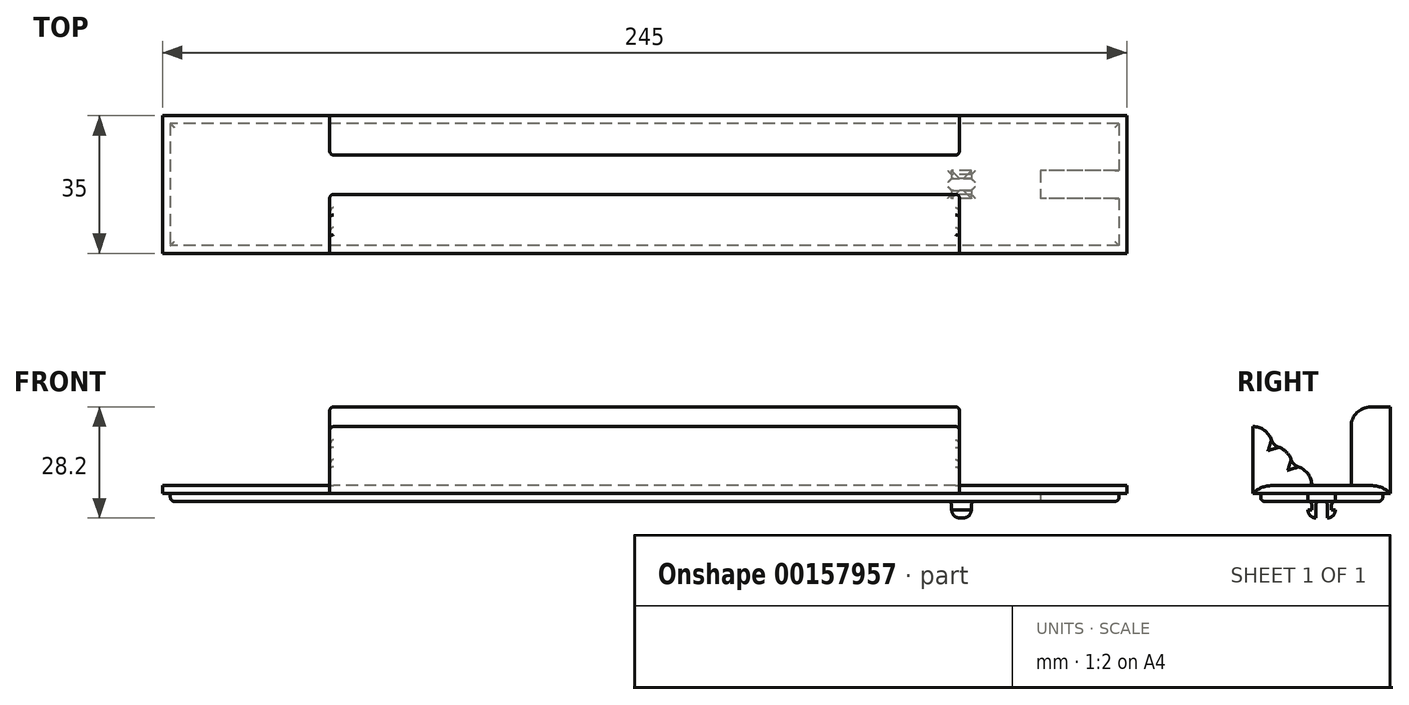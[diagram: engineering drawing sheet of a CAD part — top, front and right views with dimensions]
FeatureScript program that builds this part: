
annotation { "Feature Type Name" : "Feature", "Feature Type Description" : "" }
export const myFeature = defineFeature(function(context is Context, id is Id, definition is map)
    precondition{}
    {
        {
            var Q0;
            Q0=qCreatedBy(makeId("Right.planeOp"),FACE);
            var sketch = newSketch(context, id + "F0", { "sketchPlane" : qUnion([Q0])});
            skPoint(sketch, "E0.middle", {"position": v(0, 0) * mm});
            skLineSegment(sketch, "E1", {"start": v(18.73, 20.16) * mm, "end": v(18.73, 20.16) * mm});
            skLineSegment(sketch, "E2.bottom", {"start": v(13.13, 38.98) * mm, "end": v(22.1, 38.98) * mm});
            skPoint(sketch, "E3.visualSharp", {"position": v(11.13, 38.98) * mm});
            skArc(sketch, "E3.filletArc", {"start": v(13.13, 38.98) * mm, "mid": v(11.72, 38.4) * mm, "end": v(11.13, 36.98) * mm});
            skLineSegment(sketch, "E4.bottom", {"start": v(17.5, 1) * mm, "end": v(-17.5, 1) * mm});
            skLineSegment(sketch, "E4.top", {"start": v(17.5, -1) * mm, "end": v(-17.5, -1) * mm});
            skLineSegment(sketch, "E4.left", {"start": v(17.5, 1) * mm, "end": v(17.5, -1) * mm});
            skLineSegment(sketch, "E4.right", {"start": v(-17.5, 1) * mm, "end": v(-17.5, -1) * mm});
            skLineSegment(sketch, "E5.bottom", {"start": v(17.5, 1) * mm, "end": v(7.5, 1) * mm});
            skLineSegment(sketch, "E5.top", {"start": v(17.5, 21) * mm, "end": v(12.5, 21) * mm});
            skLineSegment(sketch, "E5.left", {"start": v(17.5, 1) * mm, "end": v(17.5, 21) * mm});
            skLineSegment(sketch, "E5.right", {"start": v(7.5, 1) * mm, "end": v(7.5, 16) * mm});
            skLineSegment(sketch, "E6.bottom", {"start": v(-17.5, 1) * mm, "end": v(-12.5, 1) * mm});
            skLineSegment(sketch, "E6.top", {"start": v(-17.5, 16) * mm, "end": v(-17.5, 16) * mm});
            skLineSegment(sketch, "E6.left", {"start": v(-17.5, 1) * mm, "end": v(-17.5, 16) * mm});
            skLineSegment(sketch, "E6.right", {"start": v(-12.5, 1) * mm, "end": v(-12.5, 11) * mm});
            skLineSegment(sketch, "E7.bottom", {"start": v(-12.5, 11) * mm, "end": v(-12.5, 11) * mm});
            skLineSegment(sketch, "E7.top", {"start": v(-12.5, 1) * mm, "end": v(-7.5, 1) * mm});
            skLineSegment(sketch, "E7.left", {"start": v(-12.5, 11) * mm, "end": v(-12.5, 1) * mm});
            skLineSegment(sketch, "E7.right", {"start": v(-7.5, 6) * mm, "end": v(-7.5, 1) * mm});
            skLineSegment(sketch, "E8.bottom", {"start": v(-7.5, 6) * mm, "end": v(-7.5, 6) * mm});
            skLineSegment(sketch, "E8.top", {"start": v(-7.5, 1) * mm, "end": v(-2.5, 1) * mm});
            skLineSegment(sketch, "E8.right", {"start": v(-2.5, 1) * mm, "end": v(-2.5, 1) * mm});
            skPoint(sketch, "E9.visualSharp", {"position": v(7.5, 21) * mm});
            skArc(sketch, "E9.filletArc", {"start": v(12.5, 21) * mm, "mid": v(8.96, 19.54) * mm, "end": v(7.5, 16) * mm});
            skPoint(sketch, "E10.visualSharp", {"position": v(-2.5, 6) * mm});
            skArc(sketch, "E10.filletArc", {"start": v(-2.5, 1) * mm, "mid": v(-3.96, 4.54) * mm, "end": v(-7.5, 6) * mm});
            skPoint(sketch, "E11.visualSharp", {"position": v(-7.5, 11) * mm});
            skArc(sketch, "E11.filletArc", {"start": v(-7.5, 6) * mm, "mid": v(-8.96, 9.54) * mm, "end": v(-12.5, 11) * mm});
            skPoint(sketch, "E12.visualSharp", {"position": v(-12.5, 16) * mm});
            skArc(sketch, "E12.filletArc", {"start": v(-12.5, 11) * mm, "mid": v(-13.96, 14.54) * mm, "end": v(-17.5, 16) * mm});
            skSolve(sketch);
        }
        {
            var Q0;
            Q0=makeQuery(id+"F0.imprint","IMPRINT",FACE,{"disambiguationData":[TD([[makeQuery(id+"F0.imprint","IMPRINT",EDGE,{"derivedFrom":sQuery(id+"F0.wireOp",EDGE,"E5.top")}),1.0]])]});
            var Q1;
            Q1=makeQuery(id+"F0.imprint","IMPRINT",FACE,{"disambiguationData":[TD([[makeQuery(id+"F0.imprint","IMPRINT",EDGE,{"derivedFrom":sQuery(id+"F0.wireOp",EDGE,"E4.top")}),-1.0]])]});
            var Q2;
            {var subQ0=sQuery(id+"F0.wireOp",EDGE,"E6.left");Q2=makeQuery(id+"F0.imprint","IMPRINT",FACE,{"disambiguationData":[TD([[makeQuery(id+"F0.imprint","IMPRINT",EDGE,{"derivedFrom":subQ0}),-1.0]])]});}
            var Q3;
            {var subQ2=sQuery(id+"F0.wireOp",EDGE,"E6.right");Q3=makeQuery(id+"F0.imprint","IMPRINT",FACE,{"disambiguationData":[TD([[makeQuery(id+"F0.imprint","IMPRINT",EDGE,{"derivedFrom":subQ2}),-1.0]])]});}
            var Q4;
            {var subQ0=sQuery(id+"F0.wireOp",EDGE,"E7.right");Q4=makeQuery(id+"F0.imprint","IMPRINT",FACE,{"disambiguationData":[TD([[makeQuery(id+"F0.imprint","IMPRINT",EDGE,{"derivedFrom":subQ0}),1.0]])]});}
            extrude(context, id + "F1", {"entities" : qUnion([Q0, Q1, Q2, Q3, Q4]), "endBound" : BoundingType.SYMMETRIC, "depth" : 245 * mm});
        }
        {
            var Q0;
            Q0=makeQuery(id+"F1.opExtrude","SWEPT_FACE",FACE,{"disambiguationData":[OSD([sQuery(id+"F0.wireOp",EDGE,"E4.top")])]});
            var sketch = newSketch(context, id + "F2", { "sketchPlane" : qUnion([Q0])});
            skLineSegment(sketch, "E13.bottom", {"start": v(120.5, -15.5) * mm, "end": v(-120.5, -15.5) * mm});
            skLineSegment(sketch, "E13.top", {"start": v(120.5, 15.5) * mm, "end": v(-120.5, 15.5) * mm});
            skLineSegment(sketch, "E13.left", {"start": v(120.5, -15.5) * mm, "end": v(120.5, 15.5) * mm});
            skLineSegment(sketch, "E13.right", {"start": v(-120.5, -15.5) * mm, "end": v(-120.5, 15.5) * mm});
            skPoint(sketch, "E13.middle", {"position": v(0, 0) * mm});
            skSolve(sketch);
        }
        {
            var Q0;
            Q0=qSketchRegion(id+"F2",true);
            extrude(context, id + "F3", {"entities" : qUnion([Q0]), "operationType" : NewBodyOperationType.ADD, "depth" : 2 * mm});
        }
        {
            var Q0;
            Q0=makeQuery(id+"F3.opExtrude","CAP_FACE",FACE,{"disambiguationData":[OSD([sQuery(id+"F2.wireOp",EDGE,"E13.bottom"),sQuery(id+"F2.wireOp",EDGE,"E13.top"),sQuery(id+"F2.wireOp",EDGE,"E13.left"),sQuery(id+"F2.wireOp",EDGE,"E13.right")])],"isStart":false});
            var sketch = newSketch(context, id + "F4", { "sketchPlane" : qUnion([Q0])});
            skLineSegment(sketch, "E14.bottom", {"start": v(83, -2.5) * mm, "end": v(78, -2.5) * mm});
            skLineSegment(sketch, "E14.top", {"start": v(83, 2.5) * mm, "end": v(78, 2.5) * mm});
            skLineSegment(sketch, "E14.left", {"start": v(83, -2.5) * mm, "end": v(83, 2.5) * mm});
            skLineSegment(sketch, "E14.right", {"start": v(78, -2.5) * mm, "end": v(78, 2.5) * mm});
            skPoint(sketch, "E14.middle", {"position": v(80.5, 0) * mm});
            skPoint(sketch, "E15", {"position": v(120.5, -0.48) * mm});
            skSolve(sketch);
        }
        {
            var Q0;
            Q0=qSketchRegion(id+"F4",true);
            extrude(context, id + "F5", {"entities" : qUnion([Q0]), "operationType" : NewBodyOperationType.ADD, "depth" : 2.2 * mm});
        }
        {
            var Q0;
            Q0=makeQuery(id+"F5.opExtrude","CAP_FACE",FACE,{"disambiguationData":[OSD([sQuery(id+"F4.wireOp",EDGE,"E14.bottom"),sQuery(id+"F4.wireOp",EDGE,"E14.top"),sQuery(id+"F4.wireOp",EDGE,"E14.left"),sQuery(id+"F4.wireOp",EDGE,"E14.right")])],"isStart":false});
            var sketch = newSketch(context, id + "F6", { "sketchPlane" : qUnion([Q0])});
            skLineSegment(sketch, "E16.bottom", {"start": v(83, 3.5) * mm, "end": v(78, 3.5) * mm});
            skLineSegment(sketch, "E16.top", {"start": v(83, -3.5) * mm, "end": v(78, -3.5) * mm});
            skLineSegment(sketch, "E16.left", {"start": v(78, 3.5) * mm, "end": v(78, -3.5) * mm});
            skLineSegment(sketch, "E16.right", {"start": v(83, 3.5) * mm, "end": v(83, -3.5) * mm});
            skPoint(sketch, "E16.middle.positionSnap0", {"position": v(83, 0) * mm});
            skPoint(sketch, "E16.centerSnap0", {"position": v(83, 0) * mm});
            skPoint(sketch, "E17", {"position": v(78, 0) * mm});
            skSolve(sketch);
        }
        {
            var Q0;
            Q0=qSketchRegion(id+"F6",true);
            extrude(context, id + "F7", {"entities" : qUnion([Q0]), "operationType" : NewBodyOperationType.ADD, "depth" : 2 * mm});
        }
        {
            var Q0;
            Q0=makeQuery(id+"F7.opExtrude","CAP_FACE",FACE,{"disambiguationData":[OSD([sQuery(id+"F6.wireOp",EDGE,"E16.bottom"),sQuery(id+"F6.wireOp",EDGE,"E16.top"),sQuery(id+"F6.wireOp",EDGE,"E16.left"),sQuery(id+"F6.wireOp",EDGE,"E16.right")])],"isStart":false});
            var sketch = newSketch(context, id + "F8", { "sketchPlane" : qUnion([Q0])});
            skLineSegment(sketch, "E18.bottom", {"start": v(83, 1.5) * mm, "end": v(78, 1.5) * mm});
            skLineSegment(sketch, "E18.top", {"start": v(83, -1.5) * mm, "end": v(78, -1.5) * mm});
            skLineSegment(sketch, "E18.left", {"start": v(78, 1.5) * mm, "end": v(78, -1.5) * mm});
            skLineSegment(sketch, "E18.right", {"start": v(83, 1.5) * mm, "end": v(83, -1.5) * mm});
            skLineSegment(sketch, "E19.bottom", {"start": v(39.5, -3.5) * mm, "end": v(36.5, -3.5) * mm});
            skSolve(sketch);
        }
        {
            var Q0;
            Q0=makeQuery(id+"F8.imprint","IMPRINT",FACE,{"disambiguationData":[TD([[makeQuery(id+"F8.imprint","IMPRINT",EDGE,{"derivedFrom":sQuery(id+"F8.wireOp",EDGE,"E18.bottom")}),1.0]])]});
            extrude(context, id + "F9", {"entities" : qUnion([Q0]), "operationType" : NewBodyOperationType.REMOVE, "oppositeDirection" : true, "depth" : 4.2 * mm});
        }
        {
            var Q0;
            {var subQ0=sQuery(id+"F6.wireOp",EDGE,"E16.right");var subQ1=sQuery(id+"F6.wireOp",EDGE,"E16.top");var subQ3=makeQuery(id+"F7.opExtrude","CAP_EDGE",EDGE,{"disambiguationData":[OSD([subQ0])],"isStart":false});Q0=makeQuery(id+"F9.boolean.opBoolean","SPLIT",EDGE,{"disambiguationData":[TD([makeQuery(id+"F7.opExtrude","SWEPT_FACE",FACE,{"disambiguationData":[OSD([subQ1])]})])],"derivedFrom":subQ3});}
            var Q1;
            {var subQ0=sQuery(id+"F6.wireOp",EDGE,"E16.right");var subQ1=sQuery(id+"F6.wireOp",EDGE,"E16.top");var subQ3=makeQuery(id+"F7.opExtrude","CAP_EDGE",EDGE,{"disambiguationData":[OSD([subQ1])],"isStart":false});Q1=makeQuery(id+"F9.boolean.opBoolean","SPLIT",EDGE,{"disambiguationData":[TD([makeQuery(id+"F7.opExtrude","SWEPT_FACE",FACE,{"disambiguationData":[OSD([subQ0])]})])],"derivedFrom":subQ3});}
            var Q2;
            {var subQ0=sQuery(id+"F6.wireOp",EDGE,"E16.bottom");var subQ1=sQuery(id+"F6.wireOp",EDGE,"E16.right");var subQ3=makeQuery(id+"F7.opExtrude","CAP_EDGE",EDGE,{"disambiguationData":[OSD([subQ1])],"isStart":false});Q2=makeQuery(id+"F9.boolean.opBoolean","SPLIT",EDGE,{"disambiguationData":[TD([makeQuery(id+"F7.opExtrude","SWEPT_FACE",FACE,{"disambiguationData":[OSD([subQ0])]})])],"derivedFrom":subQ3});}
            var Q3;
            {var subQ0=sQuery(id+"F6.wireOp",EDGE,"E16.bottom");var subQ1=sQuery(id+"F6.wireOp",EDGE,"E16.right");var subQ3=makeQuery(id+"F7.opExtrude","CAP_EDGE",EDGE,{"disambiguationData":[OSD([subQ0])],"isStart":false});Q3=makeQuery(id+"F9.boolean.opBoolean","SPLIT",EDGE,{"disambiguationData":[TD([makeQuery(id+"F7.opExtrude","SWEPT_FACE",FACE,{"disambiguationData":[OSD([subQ1])]})])],"derivedFrom":subQ3});}
            var Q4;
            {var subQ0=sQuery(id+"F6.wireOp",EDGE,"E16.bottom");var subQ1=sQuery(id+"F6.wireOp",EDGE,"E16.left");var subQ3=makeQuery(id+"F7.opExtrude","CAP_EDGE",EDGE,{"disambiguationData":[OSD([subQ0])],"isStart":false});Q4=makeQuery(id+"F9.boolean.opBoolean","SPLIT",EDGE,{"disambiguationData":[TD([makeQuery(id+"F7.opExtrude","SWEPT_FACE",FACE,{"disambiguationData":[OSD([subQ1])]})])],"derivedFrom":subQ3});}
            var Q5;
            {var subQ0=sQuery(id+"F6.wireOp",EDGE,"E16.bottom");var subQ1=sQuery(id+"F6.wireOp",EDGE,"E16.left");var subQ3=makeQuery(id+"F7.opExtrude","CAP_EDGE",EDGE,{"disambiguationData":[OSD([subQ1])],"isStart":false});Q5=makeQuery(id+"F9.boolean.opBoolean","SPLIT",EDGE,{"disambiguationData":[TD([makeQuery(id+"F7.opExtrude","SWEPT_FACE",FACE,{"disambiguationData":[OSD([subQ0])]})])],"derivedFrom":subQ3});}
            var Q6;
            {var subQ0=sQuery(id+"F6.wireOp",EDGE,"E16.left");var subQ1=sQuery(id+"F6.wireOp",EDGE,"E16.top");var subQ3=makeQuery(id+"F7.opExtrude","CAP_EDGE",EDGE,{"disambiguationData":[OSD([subQ0])],"isStart":false});Q6=makeQuery(id+"F9.boolean.opBoolean","SPLIT",EDGE,{"disambiguationData":[TD([makeQuery(id+"F7.opExtrude","SWEPT_FACE",FACE,{"disambiguationData":[OSD([subQ1])]})])],"derivedFrom":subQ3});}
            var Q7;
            {var subQ0=sQuery(id+"F6.wireOp",EDGE,"E16.left");var subQ1=sQuery(id+"F6.wireOp",EDGE,"E16.top");var subQ3=makeQuery(id+"F7.opExtrude","CAP_EDGE",EDGE,{"disambiguationData":[OSD([subQ1])],"isStart":false});Q7=makeQuery(id+"F9.boolean.opBoolean","SPLIT",EDGE,{"disambiguationData":[TD([makeQuery(id+"F7.opExtrude","SWEPT_FACE",FACE,{"disambiguationData":[OSD([subQ0])]})])],"derivedFrom":subQ3});}
            fillet(context, id + "F10", {"entities" : qUnion([Q0, Q1, Q2, Q3, Q4, Q5, Q6, Q7]), "radius" : 2 * mm, "tangentPropagation" : true, "allowEdgeOverflow" : false});
        }
        {
            var Q0;
            Q0=makeQuery(id+"F9.boolean.opBoolean","MERGE",FACE,{"derivedFrom":[makeQuery(id+"F3.opExtrude","CAP_FACE",FACE,{"disambiguationData":[OSD([sQuery(id+"F2.wireOp",EDGE,"E13.bottom"),sQuery(id+"F2.wireOp",EDGE,"E13.top"),sQuery(id+"F2.wireOp",EDGE,"E13.left"),sQuery(id+"F2.wireOp",EDGE,"E13.right")])],"isStart":false}),makeQuery(id+"F9.opExtrude","CAP_FACE",FACE,{"disambiguationData":[OSD([sQuery(id+"F8.wireOp",EDGE,"E18.bottom"),sQuery(id+"F8.wireOp",EDGE,"E18.top"),sQuery(id+"F8.wireOp",EDGE,"E18.left"),sQuery(id+"F8.wireOp",EDGE,"E18.right")])],"isStart":false})]});
            fillet(context, id + "F11", {"entities" : qUnion([Q0]), "radius" : 1 * mm, "tangentPropagation" : true, "allowEdgeOverflow" : false});
        }
        {
            var Q0;
            Q0=makeQuery(id+"F1.opExtrude","CAP_FACE",FACE,{"disambiguationData":[OSD([sQuery(id+"F0.wireOp",EDGE,"E4.bottom"),sQuery(id+"F0.wireOp",EDGE,"E4.top"),sQuery(id+"F0.wireOp",EDGE,"E4.left"),sQuery(id+"F0.wireOp",EDGE,"E4.right"),sQuery(id+"F0.wireOp",EDGE,"E5.top"),sQuery(id+"F0.wireOp",EDGE,"E5.left"),sQuery(id+"F0.wireOp",EDGE,"E5.right"),sQuery(id+"F0.wireOp",EDGE,"E6.left"),sQuery(id+"F0.wireOp",EDGE,"E9.filletArc"),sQuery(id+"F0.wireOp",EDGE,"E10.filletArc"),sQuery(id+"F0.wireOp",EDGE,"E11.filletArc"),sQuery(id+"F0.wireOp",EDGE,"E12.filletArc")])],"isStart":false});
            var sketch = newSketch(context, id + "F12", { "sketchPlane" : qUnion([Q0])});
            skLineSegment(sketch, "E20.bottom", {"start": v(18.32, 21.85) * mm, "end": v(-19.38, 21.85) * mm});
            skLineSegment(sketch, "E20.top", {"start": v(18.32, 1) * mm, "end": v(-19.38, 1) * mm});
            skLineSegment(sketch, "E20.left", {"start": v(18.32, 21.85) * mm, "end": v(18.32, 1) * mm});
            skLineSegment(sketch, "E20.right", {"start": v(-19.38, 21.85) * mm, "end": v(-19.38, 1) * mm});
            skSolve(sketch);
        }
        {
            var Q0;
            Q0=qSketchRegion(id+"F12",true);
            extrude(context, id + "F13", {"entities" : qUnion([Q0]), "operationType" : NewBodyOperationType.REMOVE, "oppositeDirection" : true, "depth" : 42.5 * mm});
        }
        {
            var Q0;
            Q0=makeQuery(id+"F1.opExtrude","CAP_FACE",FACE,{"disambiguationData":[OSD([sQuery(id+"F0.wireOp",EDGE,"E4.bottom"),sQuery(id+"F0.wireOp",EDGE,"E4.top"),sQuery(id+"F0.wireOp",EDGE,"E4.left"),sQuery(id+"F0.wireOp",EDGE,"E4.right"),sQuery(id+"F0.wireOp",EDGE,"E5.top"),sQuery(id+"F0.wireOp",EDGE,"E5.left"),sQuery(id+"F0.wireOp",EDGE,"E5.right"),sQuery(id+"F0.wireOp",EDGE,"E6.left"),sQuery(id+"F0.wireOp",EDGE,"E9.filletArc"),sQuery(id+"F0.wireOp",EDGE,"E10.filletArc"),sQuery(id+"F0.wireOp",EDGE,"E11.filletArc"),sQuery(id+"F0.wireOp",EDGE,"E12.filletArc")])],"isStart":true});
            var sketch = newSketch(context, id + "F14", { "sketchPlane" : qUnion([Q0])});
            skLineSegment(sketch, "E21.bottom", {"start": v(-18.97, 22.74) * mm, "end": v(19.2, 22.74) * mm});
            skLineSegment(sketch, "E21.top", {"start": v(-18.97, 1) * mm, "end": v(19.2, 1) * mm});
            skLineSegment(sketch, "E21.left", {"start": v(-18.97, 22.74) * mm, "end": v(-18.97, 1) * mm});
            skLineSegment(sketch, "E21.right", {"start": v(19.2, 22.74) * mm, "end": v(19.2, 1) * mm});
            skSolve(sketch);
        }
        {
            var Q0;
            Q0=qSketchRegion(id+"F14",true);
            extrude(context, id + "F15", {"entities" : qUnion([Q0]), "operationType" : NewBodyOperationType.REMOVE, "oppositeDirection" : true, "depth" : 42.5 * mm});
        }
        {
            var Q0;
            Q0=makeQuery(id+"F13.boolean.opBoolean","INTERSECT",EDGE,{"derivedFrom":[makeQuery(id+"F1.opExtrude","SWEPT_FACE",FACE,{"disambiguationData":[OSD([sQuery(id+"F0.wireOp",EDGE,"E4.left"),sQuery(id+"F0.wireOp",EDGE,"E5.left")])]}),makeQuery(id+"F13.opExtrude","SWEPT_FACE",FACE,{"disambiguationData":[OSD([sQuery(id+"F12.wireOp",EDGE,"E20.top")])]})]});
            var Q1;
            Q1=makeQuery(id+"F13.boolean.opBoolean","MERGE",EDGE,{"derivedFrom":[makeQuery(id+"F1.opExtrude","CAP_EDGE",EDGE,{"disambiguationData":[OSD([sQuery(id+"F0.wireOp",EDGE,"E4.bottom")])],"isStart":false})],"fromTools":[makeQuery(id+"F13.opExtrude","CAP_EDGE",EDGE,{"disambiguationData":[OSD([sQuery(id+"F12.wireOp",EDGE,"E20.top")])],"isStart":true})]});
            var Q2;
            Q2=makeQuery(id+"F13.boolean.opBoolean","INTERSECT",EDGE,{"derivedFrom":[makeQuery(id+"F1.opExtrude","SWEPT_FACE",FACE,{"disambiguationData":[OSD([sQuery(id+"F0.wireOp",EDGE,"E4.right"),sQuery(id+"F0.wireOp",EDGE,"E6.left")])]}),makeQuery(id+"F13.opExtrude","SWEPT_FACE",FACE,{"disambiguationData":[OSD([sQuery(id+"F12.wireOp",EDGE,"E20.top")])]})]});
            var Q3;
            Q3=makeQuery(id+"F15.boolean.opBoolean","INTERSECT",EDGE,{"derivedFrom":[makeQuery(id+"F1.opExtrude","SWEPT_FACE",FACE,{"disambiguationData":[OSD([sQuery(id+"F0.wireOp",EDGE,"E4.left"),sQuery(id+"F0.wireOp",EDGE,"E5.left")])]}),makeQuery(id+"F15.opExtrude","SWEPT_FACE",FACE,{"disambiguationData":[OSD([sQuery(id+"F14.wireOp",EDGE,"E21.top")])]})]});
            var Q4;
            Q4=makeQuery(id+"F15.boolean.opBoolean","MERGE",EDGE,{"derivedFrom":[makeQuery(id+"F1.opExtrude","CAP_EDGE",EDGE,{"disambiguationData":[OSD([sQuery(id+"F0.wireOp",EDGE,"E4.bottom")])],"isStart":true})],"fromTools":[makeQuery(id+"F15.opExtrude","CAP_EDGE",EDGE,{"disambiguationData":[OSD([sQuery(id+"F14.wireOp",EDGE,"E21.top")])],"isStart":true})]});
            var Q5;
            Q5=makeQuery(id+"F15.boolean.opBoolean","INTERSECT",EDGE,{"derivedFrom":[makeQuery(id+"F1.opExtrude","SWEPT_FACE",FACE,{"disambiguationData":[OSD([sQuery(id+"F0.wireOp",EDGE,"E4.right"),sQuery(id+"F0.wireOp",EDGE,"E6.left")])]}),makeQuery(id+"F15.opExtrude","SWEPT_FACE",FACE,{"disambiguationData":[OSD([sQuery(id+"F14.wireOp",EDGE,"E21.top")])]})]});
            fillet(context, id + "F16", {"entities" : qUnion([Q0, Q1, Q2, Q3, Q4, Q5]), "radius" : 7 * mm, "tangentPropagation" : true, "allowEdgeOverflow" : false});
        }
        {
            var Q0;
            Q0=makeQuery(id+"F15.boolean.opBoolean","INTERSECT",EDGE,{"derivedFrom":[makeQuery(id+"F1.opExtrude","SWEPT_FACE",FACE,{"disambiguationData":[OSD([sQuery(id+"F0.wireOp",EDGE,"E9.filletArc")])]}),makeQuery(id+"F15.opExtrude","CAP_FACE",FACE,{"disambiguationData":[OSD([sQuery(id+"F14.wireOp",EDGE,"E21.bottom"),sQuery(id+"F14.wireOp",EDGE,"E21.top"),sQuery(id+"F14.wireOp",EDGE,"E21.left"),sQuery(id+"F14.wireOp",EDGE,"E21.right")])],"isStart":false})]});
            var Q1;
            Q1=makeQuery(id+"F15.boolean.opBoolean","INTERSECT",EDGE,{"derivedFrom":[makeQuery(id+"F1.opExtrude","SWEPT_FACE",FACE,{"disambiguationData":[OSD([sQuery(id+"F0.wireOp",EDGE,"E5.right")])]}),makeQuery(id+"F15.opExtrude","CAP_FACE",FACE,{"disambiguationData":[OSD([sQuery(id+"F14.wireOp",EDGE,"E21.bottom"),sQuery(id+"F14.wireOp",EDGE,"E21.top"),sQuery(id+"F14.wireOp",EDGE,"E21.left"),sQuery(id+"F14.wireOp",EDGE,"E21.right")])],"isStart":false})]});
            var Q2;
            Q2=makeQuery(id+"F15.boolean.opBoolean","INTERSECT",EDGE,{"derivedFrom":[makeQuery(id+"F1.opExtrude","SWEPT_FACE",FACE,{"disambiguationData":[OSD([sQuery(id+"F0.wireOp",EDGE,"E10.filletArc")])]}),makeQuery(id+"F15.opExtrude","CAP_FACE",FACE,{"disambiguationData":[OSD([sQuery(id+"F14.wireOp",EDGE,"E21.bottom"),sQuery(id+"F14.wireOp",EDGE,"E21.top"),sQuery(id+"F14.wireOp",EDGE,"E21.left"),sQuery(id+"F14.wireOp",EDGE,"E21.right")])],"isStart":false})]});
            var Q3;
            Q3=makeQuery(id+"F15.boolean.opBoolean","INTERSECT",EDGE,{"derivedFrom":[makeQuery(id+"F1.opExtrude","SWEPT_FACE",FACE,{"disambiguationData":[OSD([sQuery(id+"F0.wireOp",EDGE,"E11.filletArc")])]}),makeQuery(id+"F15.opExtrude","CAP_FACE",FACE,{"disambiguationData":[OSD([sQuery(id+"F14.wireOp",EDGE,"E21.bottom"),sQuery(id+"F14.wireOp",EDGE,"E21.top"),sQuery(id+"F14.wireOp",EDGE,"E21.left"),sQuery(id+"F14.wireOp",EDGE,"E21.right")])],"isStart":false})]});
            var Q4;
            Q4=makeQuery(id+"F15.boolean.opBoolean","INTERSECT",EDGE,{"derivedFrom":[makeQuery(id+"F1.opExtrude","SWEPT_FACE",FACE,{"disambiguationData":[OSD([sQuery(id+"F0.wireOp",EDGE,"E12.filletArc")])]}),makeQuery(id+"F15.opExtrude","CAP_FACE",FACE,{"disambiguationData":[OSD([sQuery(id+"F14.wireOp",EDGE,"E21.bottom"),sQuery(id+"F14.wireOp",EDGE,"E21.top"),sQuery(id+"F14.wireOp",EDGE,"E21.left"),sQuery(id+"F14.wireOp",EDGE,"E21.right")])],"isStart":false})]});
            var Q5;
            Q5=makeQuery(id+"F13.boolean.opBoolean","INTERSECT",EDGE,{"derivedFrom":[makeQuery(id+"F1.opExtrude","SWEPT_FACE",FACE,{"disambiguationData":[OSD([sQuery(id+"F0.wireOp",EDGE,"E12.filletArc")])]}),makeQuery(id+"F13.opExtrude","CAP_FACE",FACE,{"disambiguationData":[OSD([sQuery(id+"F12.wireOp",EDGE,"E20.bottom"),sQuery(id+"F12.wireOp",EDGE,"E20.top"),sQuery(id+"F12.wireOp",EDGE,"E20.left"),sQuery(id+"F12.wireOp",EDGE,"E20.right")])],"isStart":false})]});
            var Q6;
            Q6=makeQuery(id+"F13.boolean.opBoolean","INTERSECT",EDGE,{"derivedFrom":[makeQuery(id+"F1.opExtrude","SWEPT_FACE",FACE,{"disambiguationData":[OSD([sQuery(id+"F0.wireOp",EDGE,"E11.filletArc")])]}),makeQuery(id+"F13.opExtrude","CAP_FACE",FACE,{"disambiguationData":[OSD([sQuery(id+"F12.wireOp",EDGE,"E20.bottom"),sQuery(id+"F12.wireOp",EDGE,"E20.top"),sQuery(id+"F12.wireOp",EDGE,"E20.left"),sQuery(id+"F12.wireOp",EDGE,"E20.right")])],"isStart":false})]});
            var Q7;
            Q7=makeQuery(id+"F13.boolean.opBoolean","INTERSECT",EDGE,{"derivedFrom":[makeQuery(id+"F1.opExtrude","SWEPT_FACE",FACE,{"disambiguationData":[OSD([sQuery(id+"F0.wireOp",EDGE,"E10.filletArc")])]}),makeQuery(id+"F13.opExtrude","CAP_FACE",FACE,{"disambiguationData":[OSD([sQuery(id+"F12.wireOp",EDGE,"E20.bottom"),sQuery(id+"F12.wireOp",EDGE,"E20.top"),sQuery(id+"F12.wireOp",EDGE,"E20.left"),sQuery(id+"F12.wireOp",EDGE,"E20.right")])],"isStart":false})]});
            var Q8;
            Q8=makeQuery(id+"F13.boolean.opBoolean","INTERSECT",EDGE,{"derivedFrom":[makeQuery(id+"F1.opExtrude","SWEPT_FACE",FACE,{"disambiguationData":[OSD([sQuery(id+"F0.wireOp",EDGE,"E5.right")])]}),makeQuery(id+"F13.opExtrude","CAP_FACE",FACE,{"disambiguationData":[OSD([sQuery(id+"F12.wireOp",EDGE,"E20.bottom"),sQuery(id+"F12.wireOp",EDGE,"E20.top"),sQuery(id+"F12.wireOp",EDGE,"E20.left"),sQuery(id+"F12.wireOp",EDGE,"E20.right")])],"isStart":false})]});
            var Q9;
            Q9=makeQuery(id+"F13.boolean.opBoolean","INTERSECT",EDGE,{"derivedFrom":[makeQuery(id+"F1.opExtrude","SWEPT_FACE",FACE,{"disambiguationData":[OSD([sQuery(id+"F0.wireOp",EDGE,"E9.filletArc")])]}),makeQuery(id+"F13.opExtrude","CAP_FACE",FACE,{"disambiguationData":[OSD([sQuery(id+"F12.wireOp",EDGE,"E20.bottom"),sQuery(id+"F12.wireOp",EDGE,"E20.top"),sQuery(id+"F12.wireOp",EDGE,"E20.left"),sQuery(id+"F12.wireOp",EDGE,"E20.right")])],"isStart":false})]});
            fillet(context, id + "F17", {"entities" : qUnion([Q0, Q1, Q2, Q3, Q4, Q5, Q6, Q7, Q8, Q9]), "radius" : 1 * mm, "tangentPropagation" : true, "allowEdgeOverflow" : false});
        }
        {
            var Q0;
            Q0=makeQuery(id+"F9.boolean.opBoolean","MERGE",FACE,{"derivedFrom":[makeQuery(id+"F3.opExtrude","CAP_FACE",FACE,{"disambiguationData":[OSD([sQuery(id+"F2.wireOp",EDGE,"E13.bottom"),sQuery(id+"F2.wireOp",EDGE,"E13.top"),sQuery(id+"F2.wireOp",EDGE,"E13.left"),sQuery(id+"F2.wireOp",EDGE,"E13.right")])],"isStart":false}),makeQuery(id+"F9.opExtrude","CAP_FACE",FACE,{"disambiguationData":[OSD([sQuery(id+"F8.wireOp",EDGE,"E18.bottom"),sQuery(id+"F8.wireOp",EDGE,"E18.top"),sQuery(id+"F8.wireOp",EDGE,"E18.left"),sQuery(id+"F8.wireOp",EDGE,"E18.right")])],"isStart":false})]});
            var sketch = newSketch(context, id + "F18", { "sketchPlane" : qUnion([Q0])});
            skLineSegment(sketch, "E22.bottom", {"start": v(120.5, -3.5) * mm, "end": v(100.5, -3.5) * mm});
            skLineSegment(sketch, "E22.top", {"start": v(120.5, 3.5) * mm, "end": v(100.5, 3.5) * mm});
            skLineSegment(sketch, "E22.left", {"start": v(120.5, -3.5) * mm, "end": v(120.5, 3.5) * mm});
            skLineSegment(sketch, "E22.right", {"start": v(100.5, -3.5) * mm, "end": v(100.5, 3.5) * mm});
            skPoint(sketch, "E22.middle", {"position": v(110.5, 0) * mm});
            skSolve(sketch);
        }
        {
            var Q0;
            Q0=qSketchRegion(id+"F18",true);
            extrude(context, id + "F19", {"entities" : qUnion([Q0]), "operationType" : NewBodyOperationType.REMOVE, "oppositeDirection" : true, "depth" : 2 * mm});
        }
        {
            var Q0;
            Q0=makeQuery(id+"F1.opExtrude","SWEPT_EDGE",EDGE,{"disambiguationData":[OSD([sQuery(id+"F0.wireOp",EDGE,"E6.right"),sQuery(id+"F0.wireOp",EDGE,"E11.filletArc"),sQuery(id+"F0.wireOp",EDGE,"E12.filletArc")])]});
            var Q1;
            Q1=makeQuery(id+"F1.opExtrude","SWEPT_EDGE",EDGE,{"disambiguationData":[OSD([sQuery(id+"F0.wireOp",EDGE,"E7.right"),sQuery(id+"F0.wireOp",EDGE,"E10.filletArc"),sQuery(id+"F0.wireOp",EDGE,"E11.filletArc")])]});
            fillet(context, id + "F20", {"entities" : qUnion([Q0, Q1]), "radius" : 3 * mm, "tangentPropagation" : true, "allowEdgeOverflow" : false});
        }
    });
